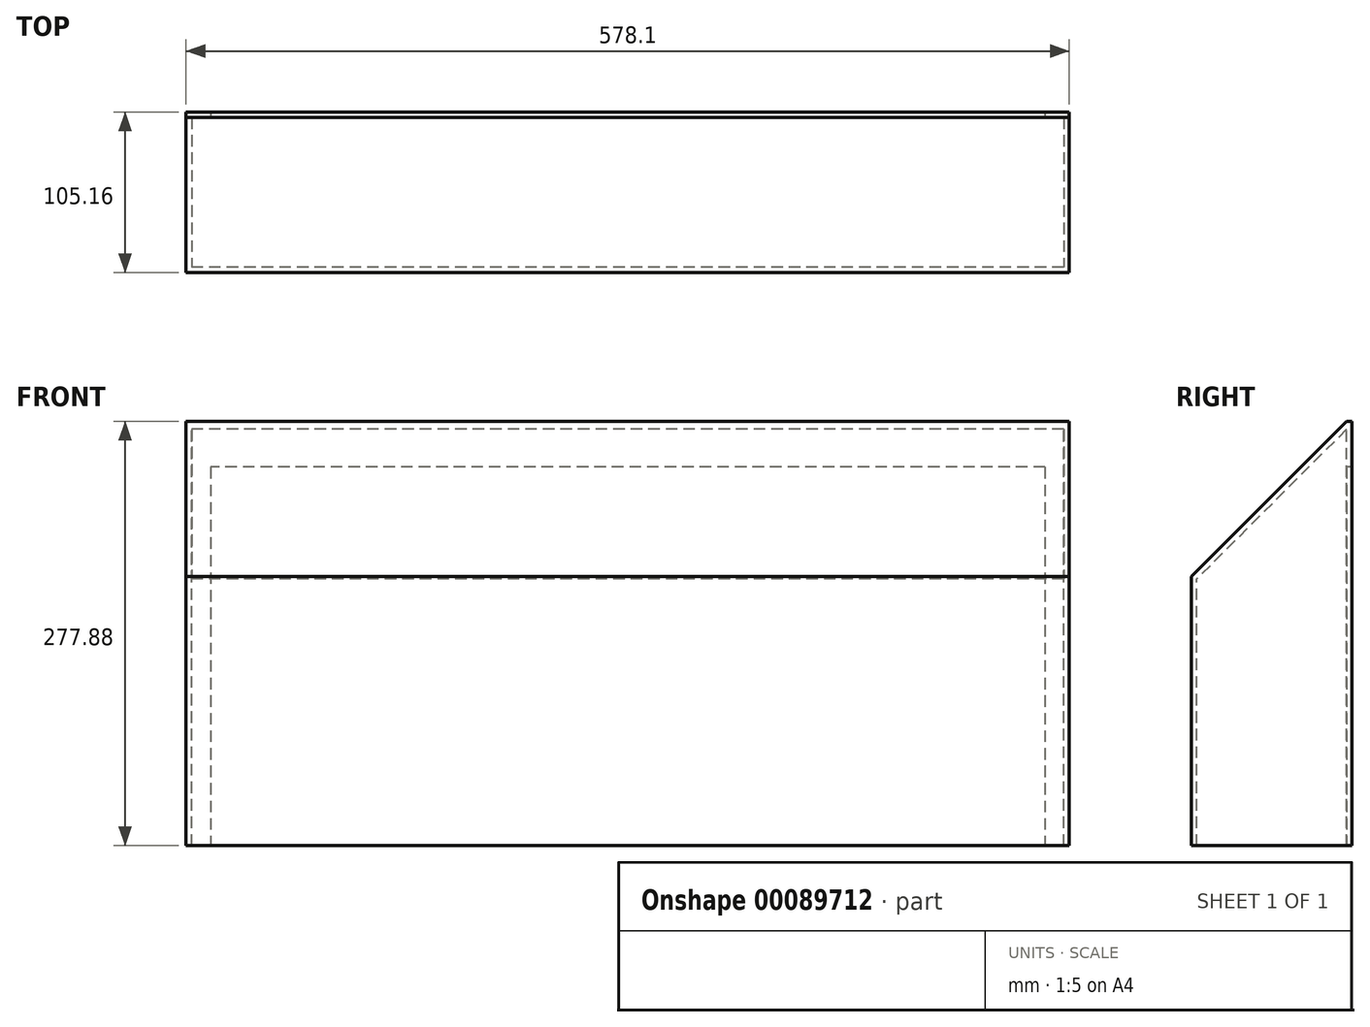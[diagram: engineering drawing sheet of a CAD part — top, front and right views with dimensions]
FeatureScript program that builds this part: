
annotation { "Feature Type Name" : "Feature", "Feature Type Description" : "" }
export const myFeature = defineFeature(function(context is Context, id is Id, definition is map)
    precondition{}
    {
        {
            var Q0;
            Q0=qCreatedBy(makeId("Right.planeOp"),FACE);
            var sketch = newSketch(context, id + "F0", { "sketchPlane" : qUnion([Q0])});
            skLineSegment(sketch, "E0", {"start": v(0, 0) * mm, "end": v(0, 277.88) * mm});
            skLineSegment(sketch, "E1", {"start": v(0, 277.88) * mm, "end": v(-101.6, 176.28) * mm});
            skLineSegment(sketch, "E2", {"start": v(0, 0) * mm, "end": v(-101.6, 0) * mm});
            skLineSegment(sketch, "E3", {"start": v(-101.6, 0) * mm, "end": v(-101.6, 176.28) * mm});
            skSolve(sketch);
        }
        {
            var Q0;
            Q0 = qSketchRegion(id + "F0", true);
            extrude(context, id + "F1", {"entities" : qUnion([Q0]), "endBound" : BoundingType.SYMMETRIC, "depth" : 578.1 * mm});
        }
        {
            var Q0;
            Q0=makeQuery(id+"F1.opExtrude","SWEPT_FACE",FACE,{"disambiguationData":[OSD([sQuery(id+"F0.wireOp",EDGE,"E0")])]});
            var Q1;
            Q1=makeQuery(id+"F1.opExtrude","SWEPT_FACE",FACE,{"disambiguationData":[OSD([sQuery(id+"F0.wireOp",EDGE,"E2")])]});
            shell(context, id + "F2", {"entities" : qUnion([Q0, Q1]), "thickness" : 3.56 * mm});
        }
        {
            var Q0;
            Q0=makeQuery(id+"F1.opExtrude","SWEPT_FACE",FACE,{"disambiguationData":[OSD([sQuery(id+"F0.wireOp",EDGE,"E0")])]});
            var sketch = newSketch(context, id + "F3", { "sketchPlane" : qUnion([Q0])});
            skLineSegment(sketch, "E4.bottom", {"start": v(-289.05, 277.88) * mm, "end": v(289.05, 277.88) * mm});
            skLineSegment(sketch, "E4.top", {"start": v(-289.05, 0) * mm, "end": v(-273.18, 0) * mm});
            skLineSegment(sketch, "E4.left", {"start": v(-289.05, 277.88) * mm, "end": v(-289.05, 0) * mm});
            skLineSegment(sketch, "E4.right", {"start": v(289.05, 277.88) * mm, "end": v(289.05, 0) * mm});
            skLineSegment(sketch, "E5.bottom", {"start": v(-273.18, 247.9) * mm, "end": v(273.05, 247.9) * mm});
            skLineSegment(sketch, "E5.left", {"start": v(-273.18, 247.9) * mm, "end": v(-273.18, 0) * mm});
            skLineSegment(sketch, "E5.right", {"start": v(273.05, 247.9) * mm, "end": v(273.05, 0) * mm});
            skLineSegment(sketch, "E6.trimOffspring", {"start": v(273.05, 0) * mm, "end": v(289.05, 0) * mm});
            skSolve(sketch);
        }
        {
            var Q0;
            Q0 = qSketchRegion(id + "F3", true);
            extrude(context, id + "F4", {"entities" : qUnion([Q0]), "operationType" : NewBodyOperationType.ADD, "depth" : 3.56 * mm});
        }
    });
